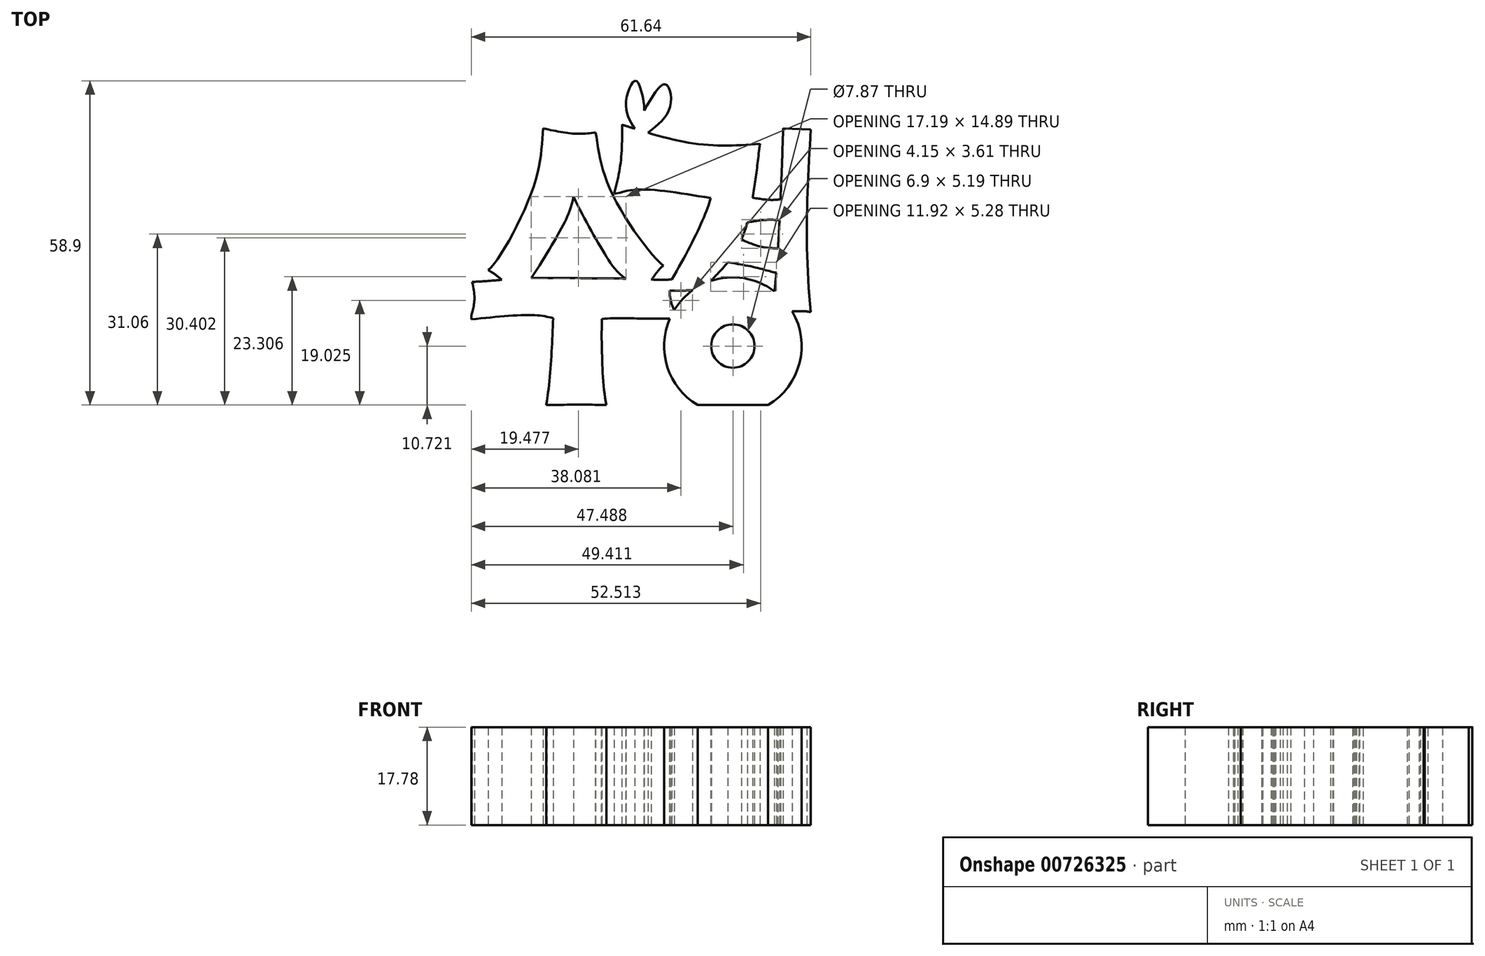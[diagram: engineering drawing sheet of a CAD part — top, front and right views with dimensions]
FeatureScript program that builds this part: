
annotation { "Feature Type Name" : "Feature", "Feature Type Description" : "" }
export const myFeature = defineFeature(function(context is Context, id is Id, definition is map)
    precondition{}
    {
        {
            var Q0;
            Q0=qCreatedBy(makeId("Top.planeOp"),FACE);
            var sketch = newSketch(context, id + "F0", { "sketchPlane" : qUnion([Q0])});
            skFitSpline(sketch, "E0", {"points": [v(9.78, 27.9) * mm, v(23.45, 24.42) * mm, v(34.78, 24.42) * mm], "startDerivative": vector(26.42, -8.36) * mm, "endDerivative": vector(23.53, 1.56) * mm});
            skFitSpline(sketch, "E1", {"points": [v(34.78, 24.42) * mm, v(31, 6.1) * mm, v(24.1, -2.32) * mm], "startDerivative": vector(-4.37, -36.06) * mm, "endDerivative": vector(-17.62, -19.75) * mm});
            skFitSpline(sketch, "E2", {"points": [v(24.1, -2.32) * mm, v(17.63, -2.1) * mm], "startDerivative": vector(-7.27, 1.16) * mm, "endDerivative": vector(-7.27, 1.16) * mm});
            skFitSpline(sketch, "E3", {"points": [v(17.63, -2.1) * mm, v(25.82, 14.58) * mm, v(25.82, 16.17) * mm], "startDerivative": vector(15.33, 25.09) * mm, "endDerivative": vector(-3.26, -0.99) * mm});
            skFitSpline(sketch, "E4", {"points": [v(25.82, 14.58) * mm, v(11.52, 16.05) * mm, v(8.33, 15.4) * mm], "startDerivative": vector(-24.55, 4.21) * mm, "endDerivative": vector(-7.62, 0.56) * mm});
            skFitSpline(sketch, "E5", {"points": [v(9.78, 27.9) * mm, v(9.5, 20.93) * mm, v(8.33, 15.4) * mm], "startDerivative": vector(-0.05, -13.67) * mm, "endDerivative": vector(-2.9, -11.3) * mm});
            skFitSpline(sketch, "E6", {"points": [v(31.93, 14.95) * mm, v(36.6, 14.26) * mm, v(39.02, 14.43) * mm], "startDerivative": vector(8.66, -1.65) * mm, "endDerivative": vector(5.33, 0.75) * mm});
            skFitSpline(sketch, "E7", {"points": [v(31.4, 9.94) * mm, v(35.9, 10.63) * mm, v(39.36, 10.46) * mm], "startDerivative": vector(8.68, 1.74) * mm, "endDerivative": vector(7.19, -0.76) * mm});
            skFitSpline(sketch, "E8", {"points": [v(30.55, 7.52) * mm, v(34.87, 5.8) * mm, v(38.84, 5.45) * mm], "startDerivative": vector(8.34, -4) * mm, "endDerivative": vector(8.26, -0.1) * mm});
            skFitSpline(sketch, "E9", {"points": [v(28.47, 3.03) * mm, v(34, 1.99) * mm, v(37.29, 1.12) * mm, v(37.86, 0.91) * mm], "startDerivative": vector(10.54, -1.95) * mm, "endDerivative": vector(-0.78, -1.9) * mm});
            skFitSpline(sketch, "E10", {"points": [v(39.02, 27.22) * mm, v(36.94, -5.1) * mm, v(36.21, -6.56) * mm], "startDerivative": vector(-1.85, -52.84) * mm, "endDerivative": vector(-4.17, -7.01) * mm});
            skFitSpline(sketch, "E11", {"points": [v(36.47, -6.13) * mm, v(41.26, -5.96) * mm, v(44.03, -6.13) * mm], "startDerivative": vector(9.2, 1.43) * mm, "endDerivative": vector(5.96, -1.57) * mm});
            skFitSpline(sketch, "E12", {"points": [v(44.03, -6.13) * mm, v(44.03, 27.05) * mm], "startDerivative": vector(-3.58, 33.95) * mm, "endDerivative": vector(2.12, 32.59) * mm});
            skFitSpline(sketch, "E13", {"points": [v(44.03, 27.05) * mm, v(39.02, 27.22) * mm], "startDerivative": vector(-5.01, 0.17) * mm, "endDerivative": vector(-5.01, 0.17) * mm});
            skCircle(sketch, "E14", {"center": v(29.88, -12.29) * mm, "radius": 12.48 * mm});
            skCircle(sketch, "E15", {"center": v(29.88, -12.29) * mm, "radius": 3.94 * mm});
            skFitSpline(sketch, "E16", {"points": [v(-4.56, 27.26) * mm, v(0.98, 26.3) * mm, v(4.99, 26.5) * mm], "startDerivative": vector(10.62, -2.35) * mm, "endDerivative": vector(8.42, 0.92) * mm});
            skFitSpline(sketch, "E17", {"points": [v(4.99, 26.5) * mm, v(7.71, 15.93) * mm, v(17.25, 2.3) * mm], "startDerivative": vector(3.24, -21.23) * mm, "endDerivative": vector(12.52, -9.95) * mm});
            skFitSpline(sketch, "E18", {"points": [v(-4.56, 27.26) * mm, v(-6.48, 16.16) * mm, v(-14.54, 1.51) * mm], "startDerivative": vector(-1.5, -21.6) * mm, "endDerivative": vector(-10.58, -8) * mm});
            skFitSpline(sketch, "E19", {"points": [v(-14.54, 1.51) * mm, v(-8.86, -2.35) * mm, v(-8.07, -1.9) * mm], "startDerivative": vector(8.07, -3.92) * mm, "endDerivative": vector(4.69, -2.84) * mm});
            skFitSpline(sketch, "E20", {"points": [v(-8.07, -1.9) * mm, v(-1.48, 8.67) * mm, v(0.97, 14.84) * mm], "startDerivative": vector(13.93, 19.65) * mm, "endDerivative": vector(3.7, 18) * mm});
            skFitSpline(sketch, "E21", {"points": [v(0.97, 14.84) * mm, v(6.64, 4.44) * mm, v(13.16, -1.55) * mm], "startDerivative": vector(9.45, -20.58) * mm, "endDerivative": vector(25.62, -11.68) * mm});
            skFitSpline(sketch, "E22", {"points": [v(13.16, -1.55) * mm, v(14.75, -0.53) * mm, v(17.25, 2.3) * mm], "startDerivative": vector(2.98, 4.47) * mm, "endDerivative": vector(5.17, 3.27) * mm});
            skFitSpline(sketch, "E23", {"points": [v(-17.45, -0.64) * mm, v(-17.18, -5.05) * mm, v(-17.6, -7.46) * mm], "startDerivative": vector(2.6, -9.42) * mm, "endDerivative": vector(0.22, -5.81) * mm});
            skFitSpline(sketch, "E24", {"points": [v(-17.6, -7.46) * mm, v(-6.25, -6.66) * mm, v(-2.73, -7.23) * mm], "startDerivative": vector(20.24, 2.14) * mm, "endDerivative": vector(8.4, -2.09) * mm});
            skFitSpline(sketch, "E25", {"points": [v(-2.73, -7.23) * mm, v(-3.3, -17.22) * mm, v(-3.98, -22.9) * mm], "startDerivative": vector(-0.72, -17.23) * mm, "endDerivative": vector(-1.16, -5.05) * mm});
            skFitSpline(sketch, "E26", {"points": [v(-17.45, -0.64) * mm, v(-8.2, 0) * mm, v(4.86, 0) * mm], "startDerivative": vector(22.19, 0.9) * mm, "endDerivative": vector(26.11, -0.19) * mm});
            skFitSpline(sketch, "E27", {"points": [v(4.86, 0) * mm, v(18.77, -0.21) * mm], "startDerivative": vector(14.53, 0.45) * mm, "endDerivative": vector(14.53, 0.45) * mm});
            skFitSpline(sketch, "E28", {"points": [v(18.77, -0.21) * mm, v(18.73, -4.5) * mm, v(19.75, -7.23) * mm], "startDerivative": vector(-2.93, -8.69) * mm, "endDerivative": vector(0.76, -4.07) * mm});
            skFitSpline(sketch, "E29", {"points": [v(19.75, -7.23) * mm, v(6.12, -7.34) * mm], "startDerivative": vector(-12.26, -0.9) * mm, "endDerivative": vector(-12.26, -0.9) * mm});
            skFitSpline(sketch, "E30", {"points": [v(6.12, -7.34) * mm, v(6.12, -13.81) * mm, v(6.92, -23.01) * mm], "startDerivative": vector(-0.62, -14.81) * mm, "endDerivative": vector(3.12, -14.48) * mm});
            skFitSpline(sketch, "E31", {"points": [v(6.92, -23.01) * mm, v(-7.84, -23.01) * mm, v(-3.98, -22.9) * mm], "startDerivative": vector(-14, 0.76) * mm, "endDerivative": vector(-8.76, 0) * mm});
            skLineSegment(sketch, "E32", {"start": v(6.92, -23.01) * mm, "end": v(36.27, -23.01) * mm});
            skLineSegment(sketch, "E33", {"start": v(-3.98, -22.9) * mm, "end": v(-3.98, -22.98) * mm});
            skFitSpline(sketch, "E34", {"points": [v(12.08, 27.19) * mm, v(10.48, 31.96) * mm, v(12.41, 35.83) * mm, v(13.77, 30.49) * mm, v(13.66, 30.49) * mm], "startDerivative": vector(-8.15, 12.76) * mm, "endDerivative": vector(-2.72, 1.71) * mm});
            skFitSpline(sketch, "E35", {"points": [v(13.77, 30.49) * mm, v(17.63, 35.26) * mm, v(18.54, 31.4) * mm, v(14.43, 26.44) * mm], "startDerivative": vector(12.24, 21.37) * mm, "endDerivative": vector(-15.14, -11.94) * mm});
            skSolve(sketch);
        }
        {
            var Q0;
            Q0=makeQuery(id+"F0.imprint","IMPRINT",FACE,{"disambiguationData":[TD([[makeQuery(id+"F0.imprint","IMPRINT",EDGE,{"derivedFrom":sQuery(id+"F0.wireOp",EDGE,"E16")}),-1.0]])]});
            var Q1;
            {var subQ0=sQuery(id+"F0.wireOp",EDGE,"E20");var subQ1=sQuery(id+"F0.wireOp",EDGE,"E19");var subQ2=makeQuery(id+"F0.imprint","INTERSECT",VERTEX,{"derivedFrom":[subQ1,subQ0]});Q1=makeQuery(id+"F0.imprint","IMPRINT",FACE,{"disambiguationData":[TD([[makeQuery(id+"F0.imprint","IMPRINT",EDGE,{"disambiguationData":[TD([[subQ2,1.0]])],"derivedFrom":subQ1}),1.0]])]});}
            var Q2;
            {var subQ0=sQuery(id+"F0.wireOp",EDGE,"E22");var subQ1=sQuery(id+"F0.wireOp",EDGE,"E21");var subQ2=makeQuery(id+"F0.imprint","INTERSECT",VERTEX,{"derivedFrom":[subQ1,subQ0]});Q2=makeQuery(id+"F0.imprint","IMPRINT",FACE,{"disambiguationData":[TD([[makeQuery(id+"F0.imprint","IMPRINT",EDGE,{"disambiguationData":[TD([[subQ2,1.0]])],"derivedFrom":subQ1}),1.0]])]});}
            var Q3;
            {var subQ0=sQuery(id+"F0.wireOp",EDGE,"E23");Q3=makeQuery(id+"F0.imprint","IMPRINT",FACE,{"disambiguationData":[TD([[makeQuery(id+"F0.imprint","IMPRINT",EDGE,{"derivedFrom":subQ0}),1.0]])]});}
            var Q4;
            {var subQ0=sQuery(id+"F0.wireOp",EDGE,"E3");var subQ1=sQuery(id+"F0.wireOp",EDGE,"E2");var subQ2=makeQuery(id+"F0.imprint","INTERSECT",VERTEX,{"derivedFrom":[subQ1,subQ0]});Q4=makeQuery(id+"F0.imprint","IMPRINT",FACE,{"disambiguationData":[TD([[makeQuery(id+"F0.imprint","IMPRINT",EDGE,{"disambiguationData":[TD([[subQ2,1.0]])],"derivedFrom":subQ1}),-1.0]])]});}
            var Q5;
            {var subQ0=sQuery(id+"F0.wireOp",EDGE,"E28");var subQ1=sQuery(id+"F0.wireOp",EDGE,"E14");var subQ2=makeQuery(id+"F0.imprint","INTERSECT",VERTEX,{"derivedFrom":[subQ1,subQ0]});Q5=makeQuery(id+"F0.imprint","IMPRINT",FACE,{"disambiguationData":[TD([[makeQuery(id+"F0.imprint","IMPRINT",EDGE,{"disambiguationData":[TD([[subQ2,-1.0]])],"derivedFrom":subQ1}),1.0]])]});}
            var Q6;
            {var subQ14=sQuery(id+"F0.wireOp",EDGE,"E0");Q6=makeQuery(id+"F0.imprint","IMPRINT",FACE,{"disambiguationData":[TD([[makeQuery(id+"F0.imprint","IMPRINT",EDGE,{"derivedFrom":subQ14}),-1.0]])]});}
            var Q7;
            {var subQ0=sQuery(id+"F0.wireOp",EDGE,"E6");var subQ1=sQuery(id+"F0.wireOp",EDGE,"E1");var subQ2=makeQuery(id+"F0.imprint","INTERSECT",VERTEX,{"derivedFrom":[subQ1,subQ0]});Q7=makeQuery(id+"F0.imprint","IMPRINT",FACE,{"disambiguationData":[TD([[makeQuery(id+"F0.imprint","IMPRINT",EDGE,{"disambiguationData":[TD([[subQ2,-1.0]])],"derivedFrom":subQ1}),1.0]])]});}
            var Q8;
            {var subQ8=sQuery(id+"F0.wireOp",EDGE,"E12");Q8=makeQuery(id+"F0.imprint","IMPRINT",FACE,{"disambiguationData":[TD([[makeQuery(id+"F0.imprint","IMPRINT",EDGE,{"derivedFrom":subQ8}),1.0]])]});}
            var Q9;
            {var subQ0=sQuery(id+"F0.wireOp",EDGE,"E8");var subQ1=sQuery(id+"F0.wireOp",EDGE,"E1");var subQ2=makeQuery(id+"F0.imprint","INTERSECT",VERTEX,{"derivedFrom":[subQ1,subQ0]});Q9=makeQuery(id+"F0.imprint","IMPRINT",FACE,{"disambiguationData":[TD([[makeQuery(id+"F0.imprint","IMPRINT",EDGE,{"disambiguationData":[TD([[subQ2,-1.0]])],"derivedFrom":subQ1}),1.0]])]});}
            var Q10;
            {var subQ0=sQuery(id+"F0.wireOp",EDGE,"E2");var subQ1=sQuery(id+"F0.wireOp",EDGE,"E1");var subQ2=makeQuery(id+"F0.imprint","INTERSECT",VERTEX,{"derivedFrom":[subQ1,subQ0]});Q10=makeQuery(id+"F0.imprint","IMPRINT",FACE,{"disambiguationData":[TD([[makeQuery(id+"F0.imprint","IMPRINT",EDGE,{"disambiguationData":[TD([[subQ2,1.0]])],"derivedFrom":subQ1}),-1.0]])]});}
            var Q11;
            {var subQ0=sQuery(id+"F0.wireOp",EDGE,"E11");var subQ1=sQuery(id+"F0.wireOp",EDGE,"E10");var subQ2=makeQuery(id+"F0.imprint","INTERSECT",VERTEX,{"derivedFrom":[subQ1,subQ0]});Q11=makeQuery(id+"F0.imprint","IMPRINT",FACE,{"disambiguationData":[TD([[makeQuery(id+"F0.imprint","IMPRINT",EDGE,{"disambiguationData":[TD([[subQ2,1.0]])],"derivedFrom":subQ1}),1.0]])]});}
            var Q12;
            Q12=makeQuery(id+"F0.imprint","IMPRINT",FACE,{"disambiguationData":[TD([[makeQuery(id+"F0.imprint","IMPRINT",EDGE,{"derivedFrom":sQuery(id+"F0.wireOp",EDGE,"E15")}),-1.0]])]});
            var Q13;
            {var subQ0=sQuery(id+"F0.wireOp",EDGE,"E33");var subQ1=sQuery(id+"F0.wireOp",EDGE,"E31");var subQ3=makeQuery(id+"F0.imprint","INTERSECT",VERTEX,{"disambiguationData":[OD(1.0)],"derivedFrom":[subQ1,subQ0]});Q13=makeQuery(id+"F0.imprint","IMPRINT",FACE,{"disambiguationData":[TD([[makeQuery(id+"F0.imprint","IMPRINT",EDGE,{"disambiguationData":[TD([[subQ3,-1.0]])],"derivedFrom":subQ1}),1.0]])]});}
            var Q14;
            {var subQ0=sQuery(id+"F0.wireOp",EDGE,"E34");var subQ1=sQuery(id+"F0.wireOp",EDGE,"E0");var subQ2=makeQuery(id+"F0.imprint","INTERSECT",VERTEX,{"derivedFrom":[subQ1,subQ0]});Q14=makeQuery(id+"F0.imprint","IMPRINT",FACE,{"disambiguationData":[TD([[makeQuery(id+"F0.imprint","IMPRINT",EDGE,{"disambiguationData":[TD([[subQ2,-1.0]])],"derivedFrom":subQ1}),1.0]])]});}
            extrude(context, id + "F1", {"entities" : qUnion([Q0, Q1, Q2, Q3, Q4, Q5, Q6, Q7, Q8, Q9, Q10, Q11, Q12, Q13, Q14]), "depth" : 17.78 * mm, "offsetDistance" : 25.4 * mm});
        }
    });
